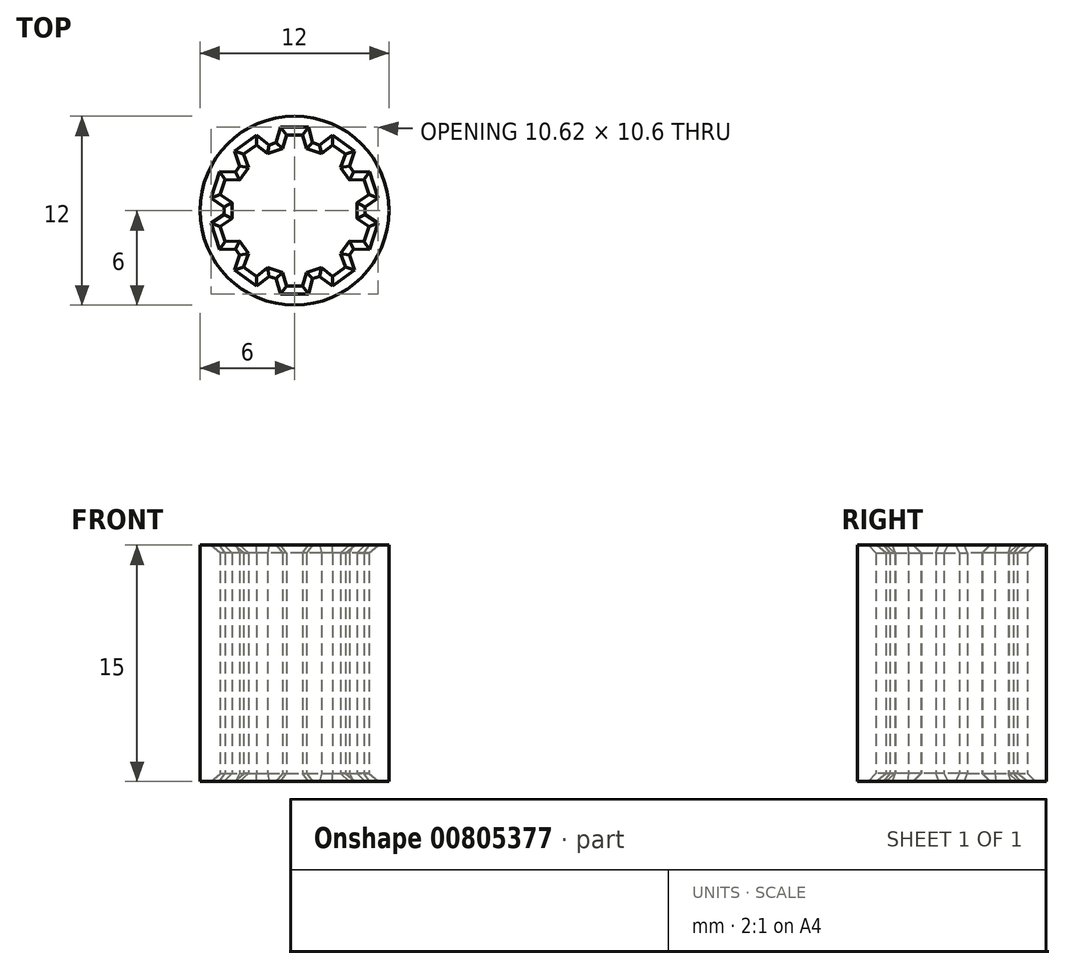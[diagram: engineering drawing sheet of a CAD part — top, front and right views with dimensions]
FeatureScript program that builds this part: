
annotation { "Feature Type Name" : "Feature", "Feature Type Description" : "" }
export const myFeature = defineFeature(function(context is Context, id is Id, definition is map)
    precondition{}
    {
        {
            var Q0;
            Q0=qCreatedBy(makeId("Top.planeOp"),FACE);
            var sketch = newSketch(context, id + "F0", { "sketchPlane" : qUnion([Q0])});
            skCircle(sketch, "E0", {"center": v(0, 0) * mm, "radius": 4 * mm, "construction": true});
            skCircle(sketch, "E1", {"center": v(0, 0) * mm, "radius": 6 * mm});
            skLineSegment(sketch, "E2", {"start": v(0.75, 3.93) * mm, "end": v(0.5, 4.8) * mm});
            skLineSegment(sketch, "E3", {"start": v(0.5, 4.8) * mm, "end": v(-0.5, 4.8) * mm});
            skLineSegment(sketch, "E4", {"start": v(-0.5, 4.8) * mm, "end": v(-0.75, 3.93) * mm});
            skLineSegment(sketch, "E5", {"start": v(0.75, 3.93) * mm, "end": v(1.7, 3.62) * mm});
            skLineSegment(sketch, "E6.1.0", {"start": v(-1.7, 3.62) * mm, "end": v(-2.42, 4.18) * mm});
            skLineSegment(sketch, "E6.1.1", {"start": v(-1.7, 3.62) * mm, "end": v(-0.75, 3.93) * mm});
            skLineSegment(sketch, "E6.1.2", {"start": v(-2.42, 4.18) * mm, "end": v(-3.23, 3.59) * mm});
            skLineSegment(sketch, "E6.1.3", {"start": v(-3.23, 3.59) * mm, "end": v(-2.92, 2.74) * mm});
            skLineSegment(sketch, "E6.2.0", {"start": v(-3.5, 1.93) * mm, "end": v(-4.41, 1.96) * mm});
            skLineSegment(sketch, "E6.2.1", {"start": v(-3.5, 1.93) * mm, "end": v(-2.92, 2.74) * mm});
            skLineSegment(sketch, "E6.2.2", {"start": v(-4.41, 1.96) * mm, "end": v(-4.72, 1) * mm});
            skLineSegment(sketch, "E6.2.3", {"start": v(-4.72, 1) * mm, "end": v(-3.97, 0.5) * mm});
            skLineSegment(sketch, "E6.3.0", {"start": v(-3.97, -0.5) * mm, "end": v(-4.72, -1) * mm});
            skLineSegment(sketch, "E6.3.1", {"start": v(-3.97, -0.5) * mm, "end": v(-3.97, 0.5) * mm});
            skLineSegment(sketch, "E6.3.2", {"start": v(-4.72, -1) * mm, "end": v(-4.41, -1.96) * mm});
            skLineSegment(sketch, "E6.3.3", {"start": v(-4.41, -1.96) * mm, "end": v(-3.5, -1.93) * mm});
            skLineSegment(sketch, "E6.4.0", {"start": v(-2.92, -2.74) * mm, "end": v(-3.23, -3.59) * mm});
            skLineSegment(sketch, "E6.4.1", {"start": v(-2.92, -2.74) * mm, "end": v(-3.5, -1.93) * mm});
            skLineSegment(sketch, "E6.4.2", {"start": v(-3.23, -3.59) * mm, "end": v(-2.42, -4.18) * mm});
            skLineSegment(sketch, "E6.4.3", {"start": v(-2.42, -4.18) * mm, "end": v(-1.7, -3.62) * mm});
            skLineSegment(sketch, "E6.5.0", {"start": v(-0.75, -3.93) * mm, "end": v(-0.5, -4.8) * mm});
            skLineSegment(sketch, "E6.5.1", {"start": v(-0.75, -3.93) * mm, "end": v(-1.7, -3.62) * mm});
            skLineSegment(sketch, "E6.5.2", {"start": v(-0.5, -4.8) * mm, "end": v(0.5, -4.8) * mm});
            skLineSegment(sketch, "E6.5.3", {"start": v(0.5, -4.8) * mm, "end": v(0.75, -3.93) * mm});
            skLineSegment(sketch, "E6.6.0", {"start": v(1.7, -3.62) * mm, "end": v(2.42, -4.18) * mm});
            skLineSegment(sketch, "E6.6.1", {"start": v(1.7, -3.62) * mm, "end": v(0.75, -3.93) * mm});
            skLineSegment(sketch, "E6.6.2", {"start": v(2.42, -4.18) * mm, "end": v(3.23, -3.59) * mm});
            skLineSegment(sketch, "E6.6.3", {"start": v(3.23, -3.59) * mm, "end": v(2.92, -2.74) * mm});
            skLineSegment(sketch, "E6.7.0", {"start": v(3.5, -1.93) * mm, "end": v(4.41, -1.96) * mm});
            skLineSegment(sketch, "E6.7.1", {"start": v(3.5, -1.93) * mm, "end": v(2.92, -2.74) * mm});
            skLineSegment(sketch, "E6.7.2", {"start": v(4.41, -1.96) * mm, "end": v(4.72, -1) * mm});
            skLineSegment(sketch, "E6.7.3", {"start": v(4.72, -1) * mm, "end": v(3.97, -0.5) * mm});
            skLineSegment(sketch, "E6.8.0", {"start": v(3.97, 0.5) * mm, "end": v(4.72, 1) * mm});
            skLineSegment(sketch, "E6.8.1", {"start": v(3.97, 0.5) * mm, "end": v(3.97, -0.5) * mm});
            skLineSegment(sketch, "E6.8.2", {"start": v(4.72, 1) * mm, "end": v(4.41, 1.96) * mm});
            skLineSegment(sketch, "E6.8.3", {"start": v(4.41, 1.96) * mm, "end": v(3.5, 1.93) * mm});
            skLineSegment(sketch, "E6.9.0", {"start": v(2.92, 2.74) * mm, "end": v(3.23, 3.59) * mm});
            skLineSegment(sketch, "E6.9.1", {"start": v(2.92, 2.74) * mm, "end": v(3.5, 1.93) * mm});
            skLineSegment(sketch, "E6.9.2", {"start": v(3.23, 3.59) * mm, "end": v(2.42, 4.18) * mm});
            skLineSegment(sketch, "E6.9.3", {"start": v(2.42, 4.18) * mm, "end": v(1.7, 3.62) * mm});
            skSolve(sketch);
        }
        {
            var Q0;
            Q0=makeQuery(id+"F0.imprint","IMPRINT",FACE,{"disambiguationData":[TD([[makeQuery(id+"F0.imprint","IMPRINT",EDGE,{"derivedFrom":sQuery(id+"F0.wireOp",EDGE,"E1")}),1.0]])]});
            extrude(context, id + "F1", {"entities" : qUnion([Q0]), "depth" : 15 * mm, "offsetDistance" : 25 * mm});
        }
        {
            var Q0;
            Q0=makeQuery(id+"F1.opExtrude","CAP_EDGE",EDGE,{"disambiguationData":[OSD([sQuery(id+"F0.wireOp",EDGE,"E6.4.0")])],"isStart":false});
            var Q1;
            Q1=makeQuery(id+"F1.opExtrude","CAP_EDGE",EDGE,{"disambiguationData":[OSD([sQuery(id+"F0.wireOp",EDGE,"E6.5.1")])],"isStart":false});
            var Q2;
            Q2=makeQuery(id+"F1.opExtrude","CAP_EDGE",EDGE,{"disambiguationData":[OSD([sQuery(id+"F0.wireOp",EDGE,"E6.11.1")])],"isStart":false});
            var Q3;
            Q3=makeQuery(id+"F1.opExtrude","CAP_EDGE",EDGE,{"disambiguationData":[OSD([sQuery(id+"F0.wireOp",EDGE,"E6.10.2")])],"isStart":false});
            var Q4;
            Q4=makeQuery(id+"F1.opExtrude","CAP_EDGE",EDGE,{"disambiguationData":[OSD([sQuery(id+"F0.wireOp",EDGE,"E6.3.2")])],"isStart":false});
            var Q5;
            Q5=makeQuery(id+"F1.opExtrude","CAP_EDGE",EDGE,{"disambiguationData":[OSD([sQuery(id+"F0.wireOp",EDGE,"E6.2.2")])],"isStart":false});
            var Q6;
            Q6=makeQuery(id+"F1.opExtrude","CAP_EDGE",EDGE,{"disambiguationData":[OSD([sQuery(id+"F0.wireOp",EDGE,"E6.4.2")])],"isStart":false});
            var Q7;
            Q7=makeQuery(id+"F1.opExtrude","CAP_EDGE",EDGE,{"disambiguationData":[OSD([sQuery(id+"F0.wireOp",EDGE,"E6.2.3")])],"isStart":false});
            var Q8;
            Q8=makeQuery(id+"F1.opExtrude","CAP_EDGE",EDGE,{"disambiguationData":[OSD([sQuery(id+"F0.wireOp",EDGE,"E6.9.2")])],"isStart":false});
            var Q9;
            Q9=makeQuery(id+"F1.opExtrude","CAP_EDGE",EDGE,{"disambiguationData":[OSD([sQuery(id+"F0.wireOp",EDGE,"E6.5.0")])],"isStart":false});
            var Q10;
            Q10=makeQuery(id+"F1.opExtrude","CAP_EDGE",EDGE,{"disambiguationData":[OSD([sQuery(id+"F0.wireOp",EDGE,"E6.4.1")])],"isStart":false});
            var Q11;
            Q11=makeQuery(id+"F1.opExtrude","CAP_EDGE",EDGE,{"disambiguationData":[OSD([sQuery(id+"F0.wireOp",EDGE,"E6.1.3")])],"isStart":false});
            var Q12;
            Q12=makeQuery(id+"F1.opExtrude","CAP_EDGE",EDGE,{"disambiguationData":[OSD([sQuery(id+"F0.wireOp",EDGE,"E6.6.1")])],"isStart":false});
            var Q13;
            Q13=makeQuery(id+"F1.opExtrude","CAP_EDGE",EDGE,{"disambiguationData":[OSD([sQuery(id+"F0.wireOp",EDGE,"E6.3.0")])],"isStart":false});
            var Q14;
            Q14=makeQuery(id+"F1.opExtrude","CAP_EDGE",EDGE,{"disambiguationData":[OSD([sQuery(id+"F0.wireOp",EDGE,"E6.9.3")])],"isStart":false});
            var Q15;
            Q15=makeQuery(id+"F1.opExtrude","CAP_EDGE",EDGE,{"disambiguationData":[OSD([sQuery(id+"F0.wireOp",EDGE,"E6.10.3")])],"isStart":false});
            var Q16;
            Q16=makeQuery(id+"F1.opExtrude","CAP_EDGE",EDGE,{"disambiguationData":[OSD([sQuery(id+"F0.wireOp",EDGE,"E6.6.3")])],"isStart":false});
            var Q17;
            Q17=makeQuery(id+"F1.opExtrude","CAP_EDGE",EDGE,{"disambiguationData":[OSD([sQuery(id+"F0.wireOp",EDGE,"E6.8.2")])],"isStart":false});
            var Q18;
            Q18=makeQuery(id+"F1.opExtrude","CAP_EDGE",EDGE,{"disambiguationData":[OSD([sQuery(id+"F0.wireOp",EDGE,"E6.8.3")])],"isStart":false});
            var Q19;
            Q19=makeQuery(id+"F1.opExtrude","CAP_EDGE",EDGE,{"disambiguationData":[OSD([sQuery(id+"F0.wireOp",EDGE,"E6.8.1")])],"isStart":false});
            var Q20;
            Q20=makeQuery(id+"F1.opExtrude","CAP_EDGE",EDGE,{"disambiguationData":[OSD([sQuery(id+"F0.wireOp",EDGE,"E6.9.0")])],"isStart":false});
            var Q21;
            Q21=makeQuery(id+"F1.opExtrude","CAP_EDGE",EDGE,{"disambiguationData":[OSD([sQuery(id+"F0.wireOp",EDGE,"E6.8.0")])],"isStart":false});
            var Q22;
            Q22=makeQuery(id+"F1.opExtrude","CAP_EDGE",EDGE,{"disambiguationData":[OSD([sQuery(id+"F0.wireOp",EDGE,"E6.6.2")])],"isStart":false});
            var Q23;
            Q23=makeQuery(id+"F1.opExtrude","CAP_EDGE",EDGE,{"disambiguationData":[OSD([sQuery(id+"F0.wireOp",EDGE,"E6.10.0")])],"isStart":false});
            var Q24;
            Q24=makeQuery(id+"F1.opExtrude","CAP_EDGE",EDGE,{"disambiguationData":[OSD([sQuery(id+"F0.wireOp",EDGE,"E6.9.1")])],"isStart":false});
            var Q25;
            Q25=makeQuery(id+"F1.opExtrude","CAP_EDGE",EDGE,{"disambiguationData":[OSD([sQuery(id+"F0.wireOp",EDGE,"E6.11.3")])],"isStart":false});
            var Q26;
            Q26=makeQuery(id+"F1.opExtrude","CAP_EDGE",EDGE,{"disambiguationData":[OSD([sQuery(id+"F0.wireOp",EDGE,"E2")])],"isStart":false});
            var Q27;
            Q27=makeQuery(id+"F1.opExtrude","CAP_EDGE",EDGE,{"disambiguationData":[OSD([sQuery(id+"F0.wireOp",EDGE,"E6.1.0")])],"isStart":false});
            var Q28;
            Q28=makeQuery(id+"F1.opExtrude","CAP_EDGE",EDGE,{"disambiguationData":[OSD([sQuery(id+"F0.wireOp",EDGE,"E3")])],"isStart":false});
            var Q29;
            Q29=makeQuery(id+"F1.opExtrude","CAP_EDGE",EDGE,{"disambiguationData":[OSD([sQuery(id+"F0.wireOp",EDGE,"E6.7.0")])],"isStart":false});
            var Q30;
            Q30=makeQuery(id+"F1.opExtrude","CAP_EDGE",EDGE,{"disambiguationData":[OSD([sQuery(id+"F0.wireOp",EDGE,"E6.11.0")])],"isStart":false});
            var Q31;
            Q31=makeQuery(id+"F1.opExtrude","CAP_EDGE",EDGE,{"disambiguationData":[OSD([sQuery(id+"F0.wireOp",EDGE,"E6.6.0")])],"isStart":false});
            var Q32;
            Q32=makeQuery(id+"F1.opExtrude","CAP_EDGE",EDGE,{"disambiguationData":[OSD([sQuery(id+"F0.wireOp",EDGE,"E6.2.1")])],"isStart":false});
            var Q33;
            Q33=makeQuery(id+"F1.opExtrude","CAP_EDGE",EDGE,{"disambiguationData":[OSD([sQuery(id+"F0.wireOp",EDGE,"E4")])],"isStart":false});
            var Q34;
            Q34=makeQuery(id+"F1.opExtrude","CAP_EDGE",EDGE,{"disambiguationData":[OSD([sQuery(id+"F0.wireOp",EDGE,"E6.5.3")])],"isStart":false});
            var Q35;
            Q35=makeQuery(id+"F1.opExtrude","CAP_EDGE",EDGE,{"disambiguationData":[OSD([sQuery(id+"F0.wireOp",EDGE,"E6.4.3")])],"isStart":false});
            var Q36;
            Q36=makeQuery(id+"F1.opExtrude","CAP_EDGE",EDGE,{"disambiguationData":[OSD([sQuery(id+"F0.wireOp",EDGE,"E6.7.3")])],"isStart":false});
            var Q37;
            Q37=makeQuery(id+"F1.opExtrude","CAP_EDGE",EDGE,{"disambiguationData":[OSD([sQuery(id+"F0.wireOp",EDGE,"E6.7.1")])],"isStart":false});
            var Q38;
            Q38=makeQuery(id+"F1.opExtrude","CAP_EDGE",EDGE,{"disambiguationData":[OSD([sQuery(id+"F0.wireOp",EDGE,"E6.5.2")])],"isStart":false});
            var Q39;
            Q39=makeQuery(id+"F1.opExtrude","CAP_EDGE",EDGE,{"disambiguationData":[OSD([sQuery(id+"F0.wireOp",EDGE,"E6.3.1")])],"isStart":false});
            var Q40;
            Q40=makeQuery(id+"F1.opExtrude","CAP_EDGE",EDGE,{"disambiguationData":[OSD([sQuery(id+"F0.wireOp",EDGE,"E6.3.3")])],"isStart":false});
            var Q41;
            Q41=makeQuery(id+"F1.opExtrude","CAP_EDGE",EDGE,{"disambiguationData":[OSD([sQuery(id+"F0.wireOp",EDGE,"E6.10.1")])],"isStart":false});
            var Q42;
            Q42=makeQuery(id+"F1.opExtrude","CAP_EDGE",EDGE,{"disambiguationData":[OSD([sQuery(id+"F0.wireOp",EDGE,"E6.7.2")])],"isStart":false});
            var Q43;
            Q43=makeQuery(id+"F1.opExtrude","CAP_EDGE",EDGE,{"disambiguationData":[OSD([sQuery(id+"F0.wireOp",EDGE,"E6.11.2")])],"isStart":false});
            var Q44;
            Q44=makeQuery(id+"F1.opExtrude","CAP_EDGE",EDGE,{"disambiguationData":[OSD([sQuery(id+"F0.wireOp",EDGE,"E6.1.2")])],"isStart":false});
            var Q45;
            Q45=makeQuery(id+"F1.opExtrude","CAP_EDGE",EDGE,{"disambiguationData":[OSD([sQuery(id+"F0.wireOp",EDGE,"E5")])],"isStart":false});
            var Q46;
            Q46=makeQuery(id+"F1.opExtrude","CAP_EDGE",EDGE,{"disambiguationData":[OSD([sQuery(id+"F0.wireOp",EDGE,"E6.2.0")])],"isStart":false});
            var Q47;
            Q47=makeQuery(id+"F1.opExtrude","CAP_EDGE",EDGE,{"disambiguationData":[OSD([sQuery(id+"F0.wireOp",EDGE,"E6.1.1")])],"isStart":false});
            var Q48;
            Q48=makeQuery(id+"F1.opExtrude","CAP_EDGE",EDGE,{"disambiguationData":[OSD([sQuery(id+"F0.wireOp",EDGE,"E6.4.2")])],"isStart":true});
            var Q49;
            Q49=makeQuery(id+"F1.opExtrude","CAP_EDGE",EDGE,{"disambiguationData":[OSD([sQuery(id+"F0.wireOp",EDGE,"E6.6.2")])],"isStart":true});
            var Q50;
            Q50=makeQuery(id+"F1.opExtrude","CAP_EDGE",EDGE,{"disambiguationData":[OSD([sQuery(id+"F0.wireOp",EDGE,"E6.5.2")])],"isStart":true});
            var Q51;
            Q51=makeQuery(id+"F1.opExtrude","CAP_EDGE",EDGE,{"disambiguationData":[OSD([sQuery(id+"F0.wireOp",EDGE,"E6.7.3")])],"isStart":true});
            var Q52;
            Q52=makeQuery(id+"F1.opExtrude","CAP_EDGE",EDGE,{"disambiguationData":[OSD([sQuery(id+"F0.wireOp",EDGE,"E6.11.1")])],"isStart":true});
            var Q53;
            Q53=makeQuery(id+"F1.opExtrude","CAP_EDGE",EDGE,{"disambiguationData":[OSD([sQuery(id+"F0.wireOp",EDGE,"E6.6.1")])],"isStart":true});
            var Q54;
            Q54=makeQuery(id+"F1.opExtrude","CAP_EDGE",EDGE,{"disambiguationData":[OSD([sQuery(id+"F0.wireOp",EDGE,"E6.11.0")])],"isStart":true});
            var Q55;
            Q55=makeQuery(id+"F1.opExtrude","CAP_EDGE",EDGE,{"disambiguationData":[OSD([sQuery(id+"F0.wireOp",EDGE,"E6.10.2")])],"isStart":true});
            var Q56;
            Q56=makeQuery(id+"F1.opExtrude","CAP_EDGE",EDGE,{"disambiguationData":[OSD([sQuery(id+"F0.wireOp",EDGE,"E6.10.1")])],"isStart":true});
            var Q57;
            Q57=makeQuery(id+"F1.opExtrude","CAP_EDGE",EDGE,{"disambiguationData":[OSD([sQuery(id+"F0.wireOp",EDGE,"E6.2.3")])],"isStart":true});
            var Q58;
            Q58=makeQuery(id+"F1.opExtrude","CAP_EDGE",EDGE,{"disambiguationData":[OSD([sQuery(id+"F0.wireOp",EDGE,"E6.11.2")])],"isStart":true});
            var Q59;
            Q59=makeQuery(id+"F1.opExtrude","CAP_EDGE",EDGE,{"disambiguationData":[OSD([sQuery(id+"F0.wireOp",EDGE,"E6.9.2")])],"isStart":true});
            var Q60;
            Q60=makeQuery(id+"F1.opExtrude","CAP_EDGE",EDGE,{"disambiguationData":[OSD([sQuery(id+"F0.wireOp",EDGE,"E6.5.0")])],"isStart":true});
            var Q61;
            Q61=makeQuery(id+"F1.opExtrude","CAP_EDGE",EDGE,{"disambiguationData":[OSD([sQuery(id+"F0.wireOp",EDGE,"E6.3.1")])],"isStart":true});
            var Q62;
            Q62=makeQuery(id+"F1.opExtrude","CAP_EDGE",EDGE,{"disambiguationData":[OSD([sQuery(id+"F0.wireOp",EDGE,"E6.7.0")])],"isStart":true});
            var Q63;
            Q63=makeQuery(id+"F1.opExtrude","CAP_EDGE",EDGE,{"disambiguationData":[OSD([sQuery(id+"F0.wireOp",EDGE,"E6.3.2")])],"isStart":true});
            var Q64;
            Q64=makeQuery(id+"F1.opExtrude","CAP_EDGE",EDGE,{"disambiguationData":[OSD([sQuery(id+"F0.wireOp",EDGE,"E6.4.0")])],"isStart":true});
            var Q65;
            Q65=makeQuery(id+"F1.opExtrude","CAP_EDGE",EDGE,{"disambiguationData":[OSD([sQuery(id+"F0.wireOp",EDGE,"E6.1.3")])],"isStart":true});
            var Q66;
            Q66=makeQuery(id+"F1.opExtrude","CAP_EDGE",EDGE,{"disambiguationData":[OSD([sQuery(id+"F0.wireOp",EDGE,"E6.5.1")])],"isStart":true});
            var Q67;
            Q67=makeQuery(id+"F1.opExtrude","CAP_EDGE",EDGE,{"disambiguationData":[OSD([sQuery(id+"F0.wireOp",EDGE,"E6.1.0")])],"isStart":true});
            var Q68;
            Q68=makeQuery(id+"F1.opExtrude","CAP_EDGE",EDGE,{"disambiguationData":[OSD([sQuery(id+"F0.wireOp",EDGE,"E6.2.2")])],"isStart":true});
            var Q69;
            Q69=makeQuery(id+"F1.opExtrude","CAP_EDGE",EDGE,{"disambiguationData":[OSD([sQuery(id+"F0.wireOp",EDGE,"E2")])],"isStart":true});
            var Q70;
            Q70=makeQuery(id+"F1.opExtrude","CAP_EDGE",EDGE,{"disambiguationData":[OSD([sQuery(id+"F0.wireOp",EDGE,"E6.9.1")])],"isStart":true});
            var Q71;
            Q71=makeQuery(id+"F1.opExtrude","CAP_EDGE",EDGE,{"disambiguationData":[OSD([sQuery(id+"F0.wireOp",EDGE,"E6.8.3")])],"isStart":true});
            var Q72;
            Q72=makeQuery(id+"F1.opExtrude","CAP_EDGE",EDGE,{"disambiguationData":[OSD([sQuery(id+"F0.wireOp",EDGE,"E5")])],"isStart":true});
            var Q73;
            Q73=makeQuery(id+"F1.opExtrude","CAP_EDGE",EDGE,{"disambiguationData":[OSD([sQuery(id+"F0.wireOp",EDGE,"E6.2.1")])],"isStart":true});
            var Q74;
            Q74=makeQuery(id+"F1.opExtrude","CAP_EDGE",EDGE,{"disambiguationData":[OSD([sQuery(id+"F0.wireOp",EDGE,"E6.6.3")])],"isStart":true});
            var Q75;
            Q75=makeQuery(id+"F1.opExtrude","CAP_EDGE",EDGE,{"disambiguationData":[OSD([sQuery(id+"F0.wireOp",EDGE,"E6.1.1")])],"isStart":true});
            var Q76;
            Q76=makeQuery(id+"F1.opExtrude","CAP_EDGE",EDGE,{"disambiguationData":[OSD([sQuery(id+"F0.wireOp",EDGE,"E6.5.3")])],"isStart":true});
            var Q77;
            Q77=makeQuery(id+"F1.opExtrude","CAP_EDGE",EDGE,{"disambiguationData":[OSD([sQuery(id+"F0.wireOp",EDGE,"E6.1.2")])],"isStart":true});
            var Q78;
            Q78=makeQuery(id+"F1.opExtrude","CAP_EDGE",EDGE,{"disambiguationData":[OSD([sQuery(id+"F0.wireOp",EDGE,"E6.3.0")])],"isStart":true});
            var Q79;
            Q79=makeQuery(id+"F1.opExtrude","CAP_EDGE",EDGE,{"disambiguationData":[OSD([sQuery(id+"F0.wireOp",EDGE,"E6.4.3")])],"isStart":true});
            var Q80;
            Q80=makeQuery(id+"F1.opExtrude","CAP_EDGE",EDGE,{"disambiguationData":[OSD([sQuery(id+"F0.wireOp",EDGE,"E6.10.3")])],"isStart":true});
            var Q81;
            Q81=makeQuery(id+"F1.opExtrude","CAP_EDGE",EDGE,{"disambiguationData":[OSD([sQuery(id+"F0.wireOp",EDGE,"E6.8.0")])],"isStart":true});
            var Q82;
            Q82=makeQuery(id+"F1.opExtrude","CAP_EDGE",EDGE,{"disambiguationData":[OSD([sQuery(id+"F0.wireOp",EDGE,"E4")])],"isStart":true});
            var Q83;
            Q83=makeQuery(id+"F1.opExtrude","CAP_EDGE",EDGE,{"disambiguationData":[OSD([sQuery(id+"F0.wireOp",EDGE,"E6.4.1")])],"isStart":true});
            var Q84;
            Q84=makeQuery(id+"F1.opExtrude","CAP_EDGE",EDGE,{"disambiguationData":[OSD([sQuery(id+"F0.wireOp",EDGE,"E6.2.0")])],"isStart":true});
            var Q85;
            Q85=makeQuery(id+"F1.opExtrude","CAP_EDGE",EDGE,{"disambiguationData":[OSD([sQuery(id+"F0.wireOp",EDGE,"E6.11.3")])],"isStart":true});
            var Q86;
            Q86=makeQuery(id+"F1.opExtrude","CAP_EDGE",EDGE,{"disambiguationData":[OSD([sQuery(id+"F0.wireOp",EDGE,"E6.8.2")])],"isStart":true});
            var Q87;
            Q87=makeQuery(id+"F1.opExtrude","CAP_EDGE",EDGE,{"disambiguationData":[OSD([sQuery(id+"F0.wireOp",EDGE,"E6.10.0")])],"isStart":true});
            var Q88;
            Q88=makeQuery(id+"F1.opExtrude","CAP_EDGE",EDGE,{"disambiguationData":[OSD([sQuery(id+"F0.wireOp",EDGE,"E6.8.1")])],"isStart":true});
            var Q89;
            Q89=makeQuery(id+"F1.opExtrude","CAP_EDGE",EDGE,{"disambiguationData":[OSD([sQuery(id+"F0.wireOp",EDGE,"E6.9.3")])],"isStart":true});
            var Q90;
            Q90=makeQuery(id+"F1.opExtrude","CAP_EDGE",EDGE,{"disambiguationData":[OSD([sQuery(id+"F0.wireOp",EDGE,"E6.6.0")])],"isStart":true});
            var Q91;
            Q91=makeQuery(id+"F1.opExtrude","CAP_EDGE",EDGE,{"disambiguationData":[OSD([sQuery(id+"F0.wireOp",EDGE,"E6.7.1")])],"isStart":true});
            var Q92;
            Q92=makeQuery(id+"F1.opExtrude","CAP_EDGE",EDGE,{"disambiguationData":[OSD([sQuery(id+"F0.wireOp",EDGE,"E3")])],"isStart":true});
            var Q93;
            Q93=makeQuery(id+"F1.opExtrude","CAP_EDGE",EDGE,{"disambiguationData":[OSD([sQuery(id+"F0.wireOp",EDGE,"E6.7.2")])],"isStart":true});
            var Q94;
            Q94=makeQuery(id+"F1.opExtrude","CAP_EDGE",EDGE,{"disambiguationData":[OSD([sQuery(id+"F0.wireOp",EDGE,"E6.9.0")])],"isStart":true});
            var Q95;
            Q95=makeQuery(id+"F1.opExtrude","CAP_EDGE",EDGE,{"disambiguationData":[OSD([sQuery(id+"F0.wireOp",EDGE,"E6.3.3")])],"isStart":true});
            chamfer(context, id + "F2", {"entities" : qUnion([Q0, Q1, Q2, Q3, Q4, Q5, Q6, Q7, Q8, Q9, Q10, Q11, Q12, Q13, Q14, Q15, Q16, Q17, Q18, Q19, Q20, Q21, Q22, Q23, Q24, Q25, Q26, Q27, Q28, Q29, Q30, Q31, Q32, Q33, Q34, Q35, Q36, Q37, Q38, Q39, Q40, Q41, Q42, Q43, Q44, Q45, Q46, Q47, Q48, Q49, Q50, Q51, Q52, Q53, Q54, Q55, Q56, Q57, Q58, Q59, Q60, Q61, Q62, Q63, Q64, Q65, Q66, Q67, Q68, Q69, Q70, Q71, Q72, Q73, Q74, Q75, Q76, Q77, Q78, Q79, Q80, Q81, Q82, Q83, Q84, Q85, Q86, Q87, Q88, Q89, Q90, Q91, Q92, Q93, Q94, Q95]), "width" : 0.5 * mm, "tangentPropagation" : true});
        }
    });
